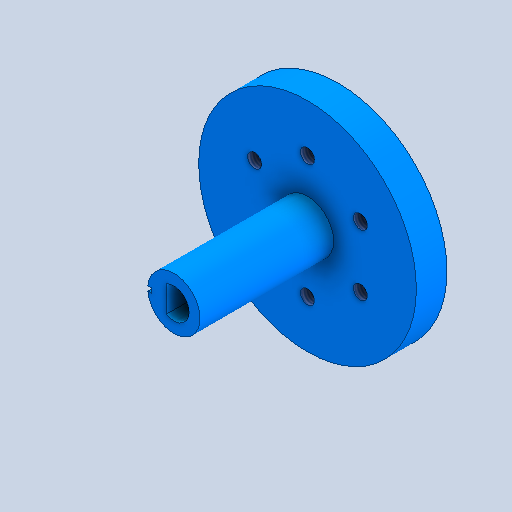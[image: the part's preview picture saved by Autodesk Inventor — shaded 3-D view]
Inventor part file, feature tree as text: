
AUTODESK INVENTOR PART (.ipt)
format: ipt  version: 2024.3 (Build 283343000, 343)  size: 189,440 bytes
history: native  units: mm
features: extrude x5, plane x4, sketch x4, hole x2, other x1, pattern_circular x1
ambient origin geometry x8: Origin, YZ Plane, XZ Plane, XY Plane, X Axis, Y Axis, Z Axis, Center Point
bodies: Body1 (feature_tree)
feature tree (17):
  other  "Sólido1"
  extrude  "Extrusión1"  TaperAngle=0.0deg  [1 undecoded]
  extrude  "Extrusión2"  Depth=2.0mm
  extrude  "Extrusión3"  Depth=10.0mm
  plane  "Plano de trabajo1"
  plane  "Plano de trabajo2"
  sketch  "Boceto5"  dims[d7=34.5mm d8=0.0mm d21=2.0mm]
  hole  "Agujero2"  [1 undecoded]
  sketch  "Boceto7"  dims[d23=3.688101mm d24=4.0mm d25=3.023mm d26=2.0mm d27=14.3117mm d28=6.0mm d29=20.594885mm d35=10.0mm]
  plane  "Plano de trabajo3"
  plane  "Plano de trabajo4"
  sketch  "Boceto9"  dims[d49=16.0mm d54=25.0mm d70=5.0mm d81=3.688101mm d82=9.0mm d83=9.0mm d84=4.0mm d85=90.0deg d86=13.0mm d87=0.0mm d88=60.0mm d89=360.0deg d91=1.2mm d92=1.0mm d93=0.0mm d94=1.0mm d95=0.0mm d53=0.5mm d55=0.5mm d56=0.872665mm d57=0.5mm d58=0.872665mm]
  hole  "Agujero6"  [1 undecoded]
  pattern_circular  "Patrón circular6"  Count=6 Angle=360.0deg
  extrude  "Extrusión6"  Depth=1.2mm
  extrude  "Extrusión7"  Depth=1.2mm TaperAngle=0.0deg
  sketch  "Boceto3"  dims[d1=8.0mm d2=0.0mm d5=0.0mm]
note: 3 required parameter values undecoded (feature->parameter linkage not recoverable at this tier; creation-order binding heuristic only, values carry confidence <= 0.55)
